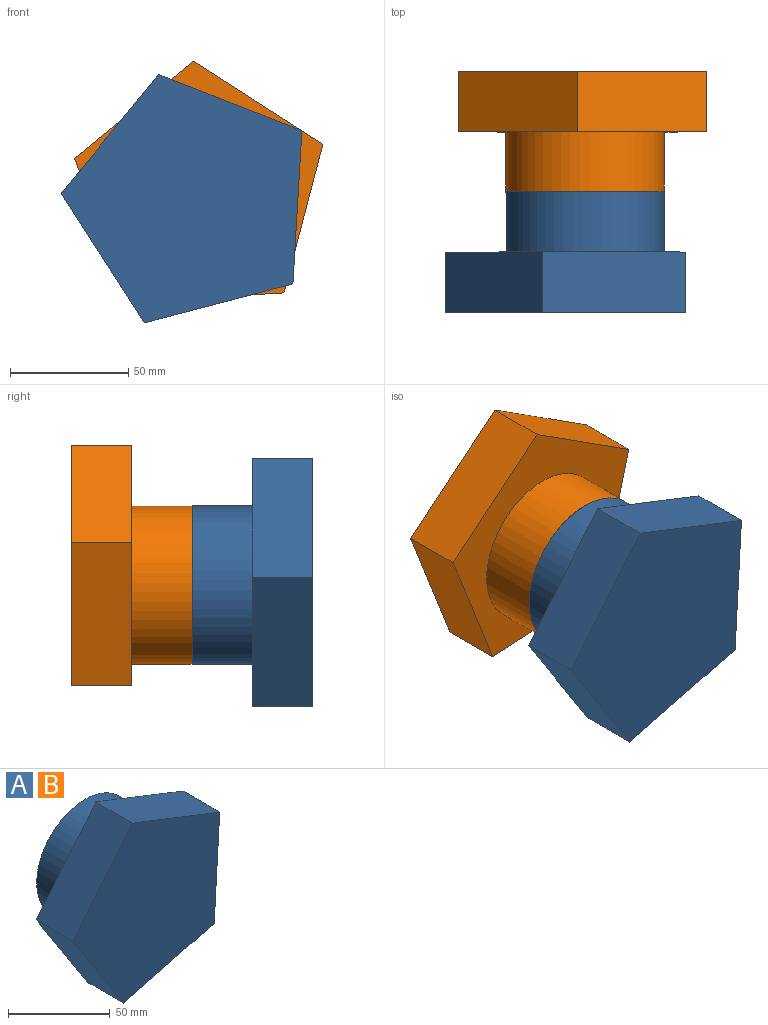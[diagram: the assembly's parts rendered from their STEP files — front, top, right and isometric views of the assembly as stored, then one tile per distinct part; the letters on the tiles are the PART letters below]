
ASSEMBLY  parts=2 mates=1
PART A: 9 faces, bbox 101.7x50.8x105 mm
  f0: cylinder r=33.43mm len=66.87mm, axis (0,1,0), area 5335.7mm2, adj f1,f8
  f1: plane 66.87x66.87mm, normal (0,1,0), area 3511.7mm2, adj f0
  f2: plane 54.72x35.06mm, normal (-0.84,0,-0.54), area 1650.7mm2, adj f3,f6,f7,f8
  f3: plane 62.88x25.4mm, normal (0.25,0,-0.97), area 1650.7mm2, adj f2,f4,f7,f8
  f4: plane 64.88x25.4mm, normal (1,0,-0.06), area 1650.7mm2, adj f3,f5,f7,f8
  f5: plane 60.53x25.4mm, normal (0.36,0,0.93), area 1650.7mm2, adj f4,f6,f7,f8
  f6: plane 50.25x41.21mm, normal (-0.77,0,0.63), area 1650.7mm2, adj f2,f5,f7,f8
  f7: plane 104.97x101.74mm, normal (0,-1,0), area 7266.4mm2, adj f2,f3,f4,f5,f6
  f8: plane 104.97x101.74mm, normal (0,1,0), area 3754.8mm2, adj f0,f2,f3,f4,f5,f6
PART B: same geometry as A
PLACE A at identity
PLACE B rot(axis=(-0.71,0,0.71),180deg) t=(0,0,0)mm
MATE fastened B.f0 <-> A.f0  axis (0,-1,0) through (0,0,0)mm
